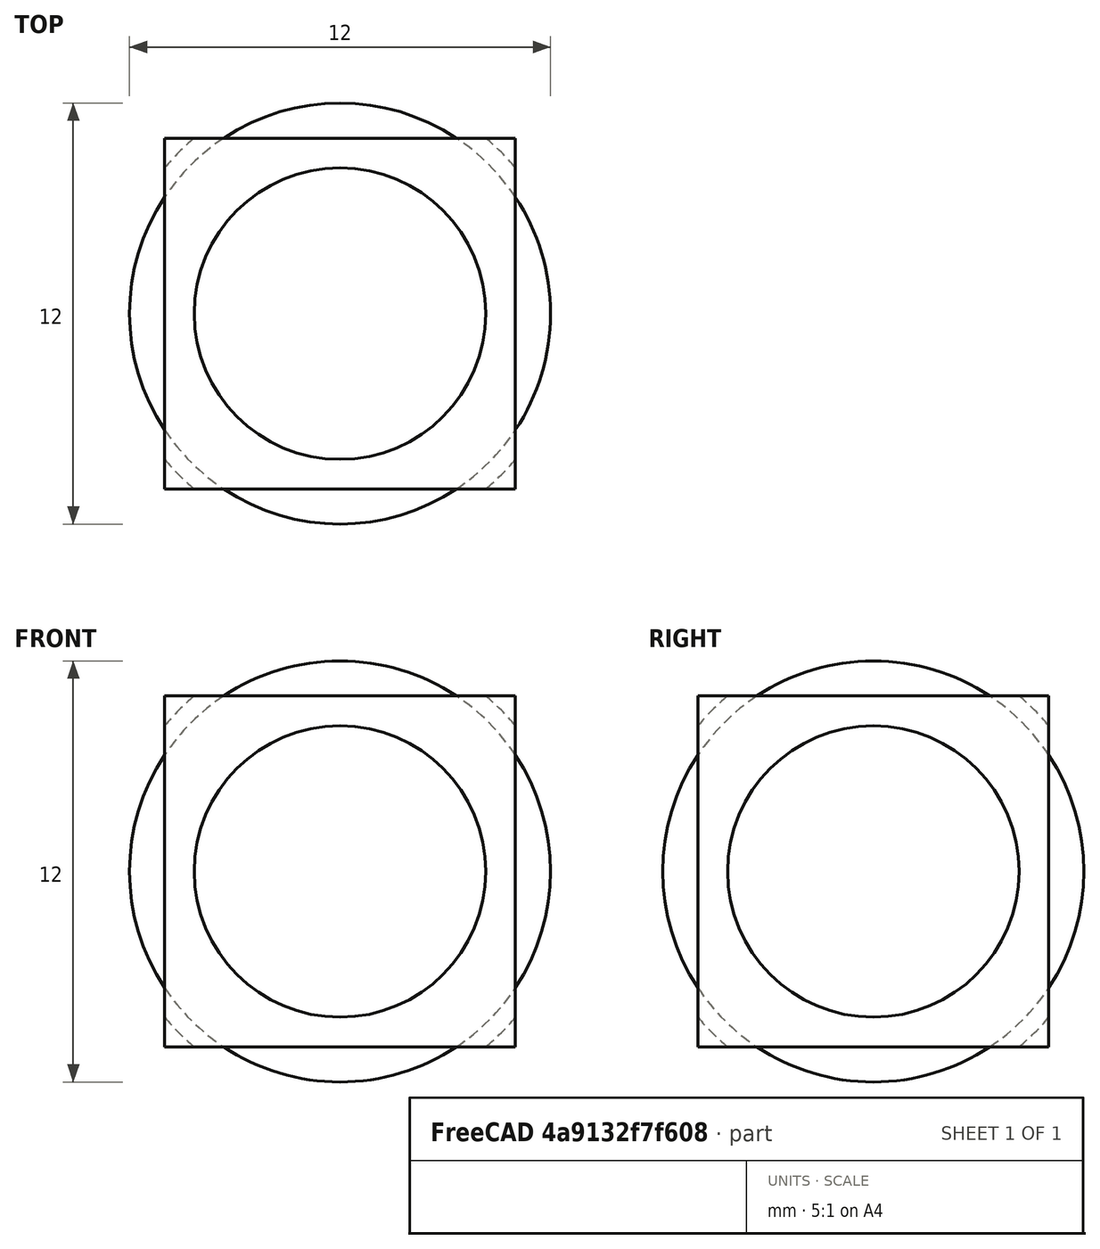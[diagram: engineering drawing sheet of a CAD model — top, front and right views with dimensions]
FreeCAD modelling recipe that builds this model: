
FCSTD DOCUMENT  (FreeCAD 0.21R33694 (Git))
Label: cartacho_repte3
License: All rights reserved
LicenseURL: http://en.wikipedia.org/wiki/All_rights_reserved
objects: Part::Cylinder×3, Part::MultiFuse×2, Part::Sphere×2, Part::Cut×2, Part::Box×1
note: 10 computed .brp shape members not serialized (recipe doc carries the construction recipe); baked Part::Feature solids carry a one-line shape summary decoded from their .brp

FEATURE [Part::Box] Box  label="Cube"
  AttacherType = Attacher::AttachEngine3D
  Height = 10
  Length = 10
  Width = 10
FEATURE [Part::Cylinder] Cylinder
  Angle = 360
  AttacherType = Attacher::AttachEngine3D
  FirstAngle = 0
  Height = 12
  Placement = pos=(5,5,-1) rot=(0,0,1;0rad)
  Radius = 4
  SecondAngle = 0
FEATURE [Part::Cylinder] Cylinder001
  Angle = 360
  AttacherType = Attacher::AttachEngine3D
  FirstAngle = 0
  Height = 12
  Placement = pos=(-1,5,5) rot=(0,1,0;1.5708rad)
  Radius = 4
  SecondAngle = 0
FEATURE [Part::MultiFuse] Fusion
  Refine = true
  Shapes = -> [Cylinder001,Cylinder]
FEATURE [Part::Cylinder] Cylinder002
  Angle = 360
  AttacherType = Attacher::AttachEngine3D
  FirstAngle = 0
  Height = 12
  Placement = pos=(5,11,5) rot=(1,0,0;1.5708rad)
  Radius = 4
  SecondAngle = 0
FEATURE [Part::MultiFuse] Fusion001
  Refine = true
  Shapes = -> [Fusion,Cylinder002,Cylinder001,Cylinder]
FEATURE [Part::Sphere] Sphere
  Angle1 = -90
  Angle2 = 90
  Angle3 = 360
  AttacherType = Attacher::AttachEngine3D
  Placement = pos=(5,5,5) rot=(0,0,1;0rad)
  Radius = 6.5
FEATURE [Part::Cut] Cut
  Base = -> Box
  Refine = true
  Tool = -> Fusion001
FEATURE [Part::Sphere] Sphere001
  Angle1 = -90
  Angle2 = 90
  Angle3 = 360
  AttacherType = Attacher::AttachEngine3D
  Placement = pos=(5,5,5) rot=(0,0,1;0rad)
  Radius = 6
FEATURE [Part::Cut] Cut001
  Base = -> Cut
  Refine = true
  Tool = -> Sphere
